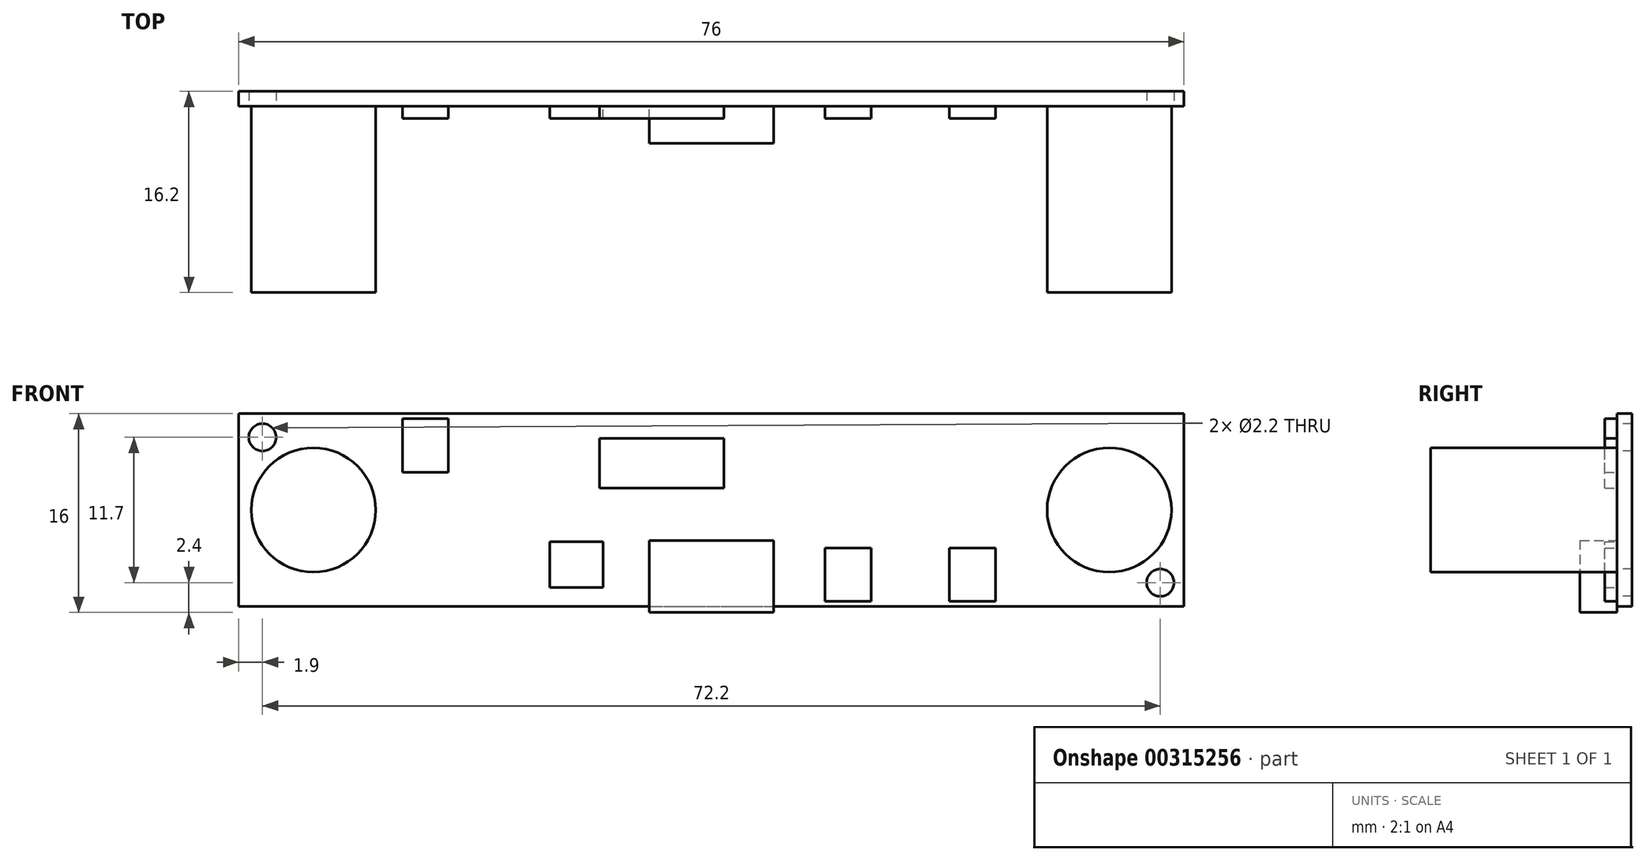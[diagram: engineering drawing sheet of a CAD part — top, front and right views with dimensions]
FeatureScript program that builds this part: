
annotation { "Feature Type Name" : "Feature", "Feature Type Description" : "" }
export const myFeature = defineFeature(function(context is Context, id is Id, definition is map)
    precondition{}
    {
        {
            var Q0;
            Q0=qCreatedBy(makeId("Front.planeOp"),FACE);
            var sketch = newSketch(context, id + "F0", { "sketchPlane" : qUnion([Q0])});
            skLineSegment(sketch, "E0.bottom", {"start": v(-38, 7.75) * mm, "end": v(38, 7.75) * mm});
            skLineSegment(sketch, "E0.top", {"start": v(-38, -7.75) * mm, "end": v(38, -7.75) * mm});
            skLineSegment(sketch, "E0.left", {"start": v(-38, 7.75) * mm, "end": v(-38, -7.75) * mm});
            skLineSegment(sketch, "E0.right", {"start": v(38, 7.75) * mm, "end": v(38, -7.75) * mm});
            skPoint(sketch, "E0.middle", {"position": v(0, 0) * mm});
            skCircle(sketch, "E1", {"center": v(36.1, -5.85) * mm, "radius": 1.1 * mm});
            skCircle(sketch, "E2.1.1", {"center": v(-36.1, 5.85) * mm, "radius": 1.1 * mm});
            skSolve(sketch);
        }
        {
            var Q0;
            Q0 = qSketchRegion(id + "F0", true);
            extrude(context, id + "F1", {"entities" : qUnion([Q0]), "oppositeDirection" : true, "depth" : 1.2 * mm});
        }
        {
            var Q0;
            Q0=qCreatedBy(makeId("Front.planeOp"),FACE);
            var sketch = newSketch(context, id + "F2", { "sketchPlane" : qUnion([Q0])});
            skLineSegment(sketch, "E3.bottom", {"start": v(-38, 7.75) * mm, "end": v(38, 7.75) * mm, "construction": true});
            skLineSegment(sketch, "E3.top", {"start": v(-38, -7.75) * mm, "end": v(38, -7.75) * mm, "construction": true});
            skLineSegment(sketch, "E3.left", {"start": v(-38, 7.75) * mm, "end": v(-38, -7.75) * mm, "construction": true});
            skLineSegment(sketch, "E3.right", {"start": v(38, 7.75) * mm, "end": v(38, -7.75) * mm, "construction": true});
            skPoint(sketch, "E3.middle", {"position": v(0, 0) * mm});
            skPoint(sketch, "E4.middle", {"position": v(0, -7.75) * mm});
            skLineSegment(sketch, "E5.bottom", {"start": v(12.85, -7.35) * mm, "end": v(9.15, -7.35) * mm});
            skLineSegment(sketch, "E5.top", {"start": v(12.85, -3.05) * mm, "end": v(9.15, -3.05) * mm});
            skLineSegment(sketch, "E5.left", {"start": v(12.85, -7.35) * mm, "end": v(12.85, -3.05) * mm});
            skLineSegment(sketch, "E5.right", {"start": v(9.15, -7.35) * mm, "end": v(9.15, -3.05) * mm});
            skPoint(sketch, "E5.middle", {"position": v(11, -5.2) * mm});
            skLineSegment(sketch, "E6.bottom", {"start": v(-21.15, 3.05) * mm, "end": v(-24.85, 3.05) * mm});
            skLineSegment(sketch, "E6.top", {"start": v(-21.15, 7.35) * mm, "end": v(-24.85, 7.35) * mm});
            skLineSegment(sketch, "E6.left", {"start": v(-21.15, 3.05) * mm, "end": v(-21.15, 7.35) * mm});
            skLineSegment(sketch, "E6.right", {"start": v(-24.85, 3.05) * mm, "end": v(-24.85, 7.35) * mm});
            skPoint(sketch, "E6.middle", {"position": v(-23, 5.2) * mm});
            skLineSegment(sketch, "E7", {"start": v(16, 2.67) * mm, "end": v(16, -12) * mm, "construction": true});
            skLineSegment(sketch, "E8.MirrorCS", {"start": v(19.15, -7.35) * mm, "end": v(19.15, -3.05) * mm});
            skLineSegment(sketch, "E9.MirrorCS", {"start": v(19.15, -3.05) * mm, "end": v(22.85, -3.05) * mm});
            skLineSegment(sketch, "E10.MirrorCS", {"start": v(22.85, -7.35) * mm, "end": v(22.85, -3.05) * mm});
            skLineSegment(sketch, "E11.MirrorCS", {"start": v(19.15, -7.35) * mm, "end": v(22.85, -7.35) * mm});
            skLineSegment(sketch, "E12.bottom", {"start": v(1, 1.75) * mm, "end": v(-9, 1.75) * mm});
            skLineSegment(sketch, "E12.top", {"start": v(1, 5.75) * mm, "end": v(-9, 5.75) * mm});
            skLineSegment(sketch, "E12.left", {"start": v(1, 1.75) * mm, "end": v(1, 5.75) * mm});
            skLineSegment(sketch, "E12.right", {"start": v(-9, 1.75) * mm, "end": v(-9, 5.75) * mm});
            skPoint(sketch, "E12.middle", {"position": v(-4, 3.75) * mm});
            skLineSegment(sketch, "E13.bottom", {"start": v(-8.7, -6.25) * mm, "end": v(-13, -6.25) * mm});
            skLineSegment(sketch, "E13.top", {"start": v(-8.7, -2.55) * mm, "end": v(-13, -2.55) * mm});
            skLineSegment(sketch, "E13.left", {"start": v(-8.7, -6.25) * mm, "end": v(-8.7, -2.55) * mm});
            skLineSegment(sketch, "E13.right", {"start": v(-13, -6.25) * mm, "end": v(-13, -2.55) * mm});
            skPoint(sketch, "E13.middle", {"position": v(-10.85, -4.4) * mm});
            skSolve(sketch);
        }
        {
            var Q0;
            Q0=qCreatedBy(makeId("Front.planeOp"),FACE);
            var sketch = newSketch(context, id + "F3", { "sketchPlane" : qUnion([Q0])});
            skLineSegment(sketch, "E14.bottom", {"start": v(-38, 7.75) * mm, "end": v(38, 7.75) * mm, "construction": true});
            skLineSegment(sketch, "E14.top", {"start": v(-38, -7.75) * mm, "end": v(38, -7.75) * mm, "construction": true});
            skLineSegment(sketch, "E14.left", {"start": v(-38, 7.75) * mm, "end": v(-38, -7.75) * mm, "construction": true});
            skLineSegment(sketch, "E14.right", {"start": v(38, 7.75) * mm, "end": v(38, -7.75) * mm, "construction": true});
            skCircle(sketch, "E15", {"center": v(32, 0) * mm, "radius": 5 * mm});
            skCircle(sketch, "E16.MirrorC", {"center": v(-32, 0) * mm, "radius": 5 * mm});
            skSolve(sketch);
        }
        {
            var Q0;
            Q0 = qSketchRegion(id + "F2", true);
            extrude(context, id + "F4", {"entities" : qUnion([Q0]), "operationType" : NewBodyOperationType.ADD, "depth" : 1 * mm});
        }
        {
            var Q0;
            Q0 = qSketchRegion(id + "F3", true);
            extrude(context, id + "F5", {"entities" : qUnion([Q0]), "operationType" : NewBodyOperationType.ADD, "depth" : 15 * mm, "offsetDistance" : 25 * mm});
        }
        {
            var Q0;
            Q0=qCreatedBy(makeId("Front.planeOp"),FACE);
            var sketch = newSketch(context, id + "F6", { "sketchPlane" : qUnion([Q0])});
            skLineSegment(sketch, "E17.bottom", {"start": v(-5, -2.45) * mm, "end": v(5, -2.45) * mm});
            skLineSegment(sketch, "E17.top", {"start": v(-5, -8.25) * mm, "end": v(5, -8.25) * mm});
            skLineSegment(sketch, "E17.left", {"start": v(-5, -2.45) * mm, "end": v(-5, -8.25) * mm});
            skLineSegment(sketch, "E17.right", {"start": v(5, -2.45) * mm, "end": v(5, -8.25) * mm});
            skSolve(sketch);
        }
        {
            var Q0;
            Q0 = qSketchRegion(id + "F6", true);
            extrude(context, id + "F7", {"entities" : qUnion([Q0]), "operationType" : NewBodyOperationType.ADD, "depth" : 3 * mm});
        }
    });
